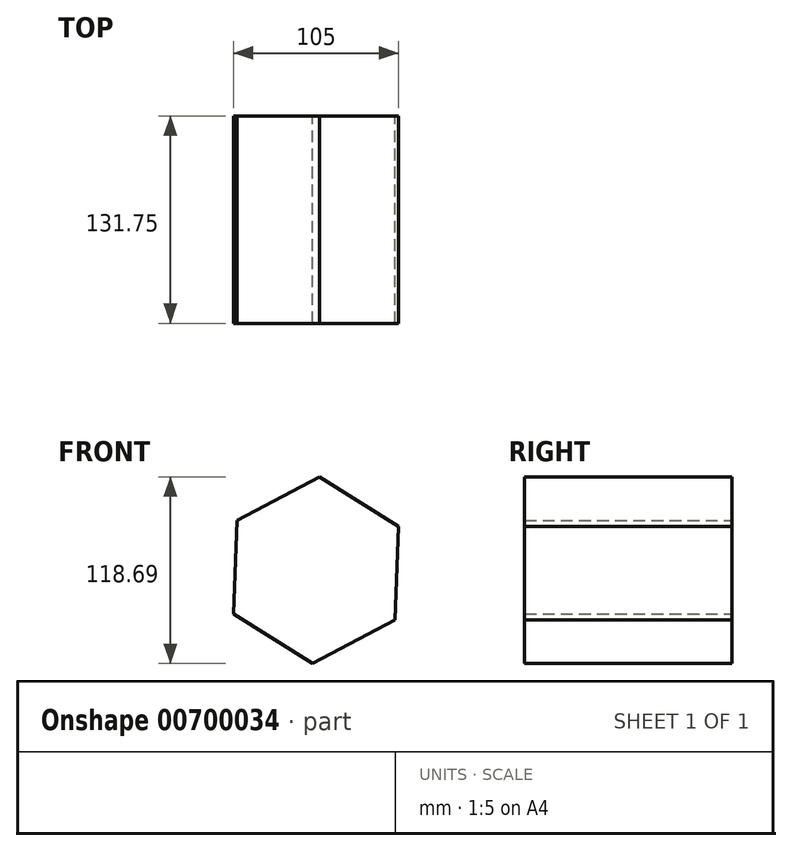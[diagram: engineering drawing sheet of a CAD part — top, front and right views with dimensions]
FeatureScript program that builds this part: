
annotation { "Feature Type Name" : "Feature", "Feature Type Description" : "" }
export const myFeature = defineFeature(function(context is Context, id is Id, definition is map)
    precondition{}
    {
        {
            var Q0;
            Q0=qCreatedBy(makeId("Front.planeOp"),FACE);
            var sketch = newSketch(context, id + "F0", { "sketchPlane" : qUnion([Q0])});
            skCircle(sketch, "E0.cCircle", {"center": v(3.52, 14.28) * mm, "radius": 59.38 * mm, "construction": true});
            skLineSegment(sketch, "E0.0", {"start": v(53.8, -17.3) * mm, "end": v(1.31, -45.06) * mm});
            skLineSegment(sketch, "E0.1", {"start": v(1.31, -45.06) * mm, "end": v(-48.98, -13.48) * mm});
            skLineSegment(sketch, "E0.2", {"start": v(-48.98, -13.48) * mm, "end": v(-46.77, 45.86) * mm});
            skLineSegment(sketch, "E0.3", {"start": v(-46.77, 45.86) * mm, "end": v(5.73, 73.63) * mm});
            skLineSegment(sketch, "E0.4", {"start": v(5.73, 73.63) * mm, "end": v(56.02, 42.04) * mm});
            skLineSegment(sketch, "E0.5", {"start": v(56.02, 42.04) * mm, "end": v(53.8, -17.3) * mm});
            skSolve(sketch);
        }
        {
            var Q0;
            Q0=makeQuery(id+"F0.imprint","IMPRINT",FACE,{"disambiguationData":[TD([[makeQuery(id+"F0.imprint","IMPRINT",EDGE,{"derivedFrom":sQuery(id+"F0.wireOp",EDGE,"E0.0")}),-1.0]])]});
            extrude(context, id + "F1", {"entities" : qUnion([Q0]), "depth" : 106.35 * mm, "offsetDistance" : 25.4 * mm});
        }
        {
            var Q0;
            Q0=makeQuery(id+"F1.opExtrude","CAP_FACE",FACE,{"disambiguationData":[OSD([sQuery(id+"F0.wireOp",EDGE,"E0.0"),sQuery(id+"F0.wireOp",EDGE,"E0.1"),sQuery(id+"F0.wireOp",EDGE,"E0.2"),sQuery(id+"F0.wireOp",EDGE,"E0.3"),sQuery(id+"F0.wireOp",EDGE,"E0.4"),sQuery(id+"F0.wireOp",EDGE,"E0.5")])],"isStart":false});
            extrude(context, id + "F2", {"entities" : qUnion([Q0]), "operationType" : NewBodyOperationType.ADD, "depth" : 25.4 * mm, "offsetDistance" : 25.4 * mm});
        }
    });
